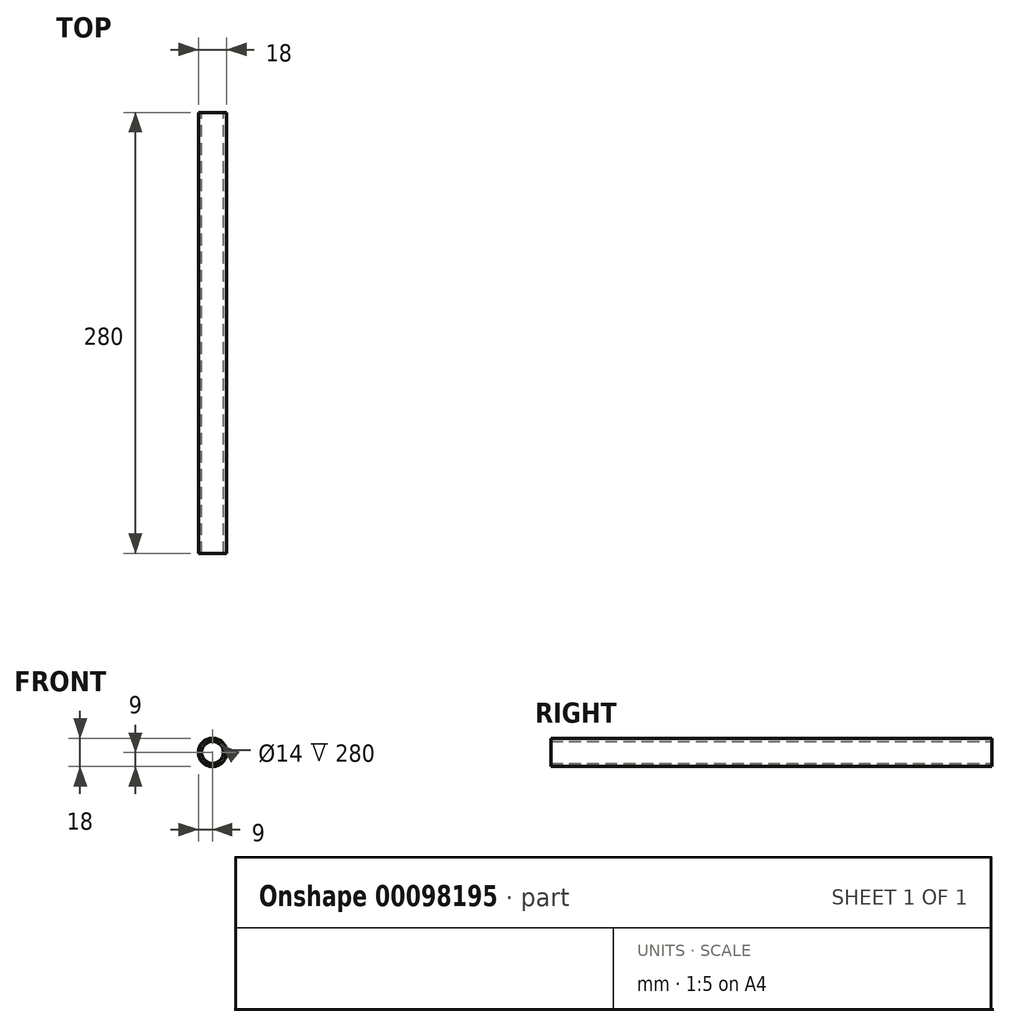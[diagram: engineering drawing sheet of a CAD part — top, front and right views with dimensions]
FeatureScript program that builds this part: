
annotation { "Feature Type Name" : "Feature", "Feature Type Description" : "" }
export const myFeature = defineFeature(function(context is Context, id is Id, definition is map)
    precondition{}
    {
        {
            var Q0;
            Q0=qCreatedBy(makeId("Front.planeOp"),FACE);
            var sketch = newSketch(context, id + "F0", { "sketchPlane" : qUnion([Q0])});
            skCircle(sketch, "E0", {"center": v(0, 0) * mm, "radius": 9 * mm});
            skCircle(sketch, "E1", {"center": v(0, 0) * mm, "radius": 7 * mm});
            skSolve(sketch);
        }
        {
            var Q0;
            Q0=qSketchRegion(id+"F0",true);
            extrude(context, id + "F1", {"entities" : qUnion([Q0]), "endBound" : BoundingType.SYMMETRIC, "depth" : 280 * mm});
        }
    });
